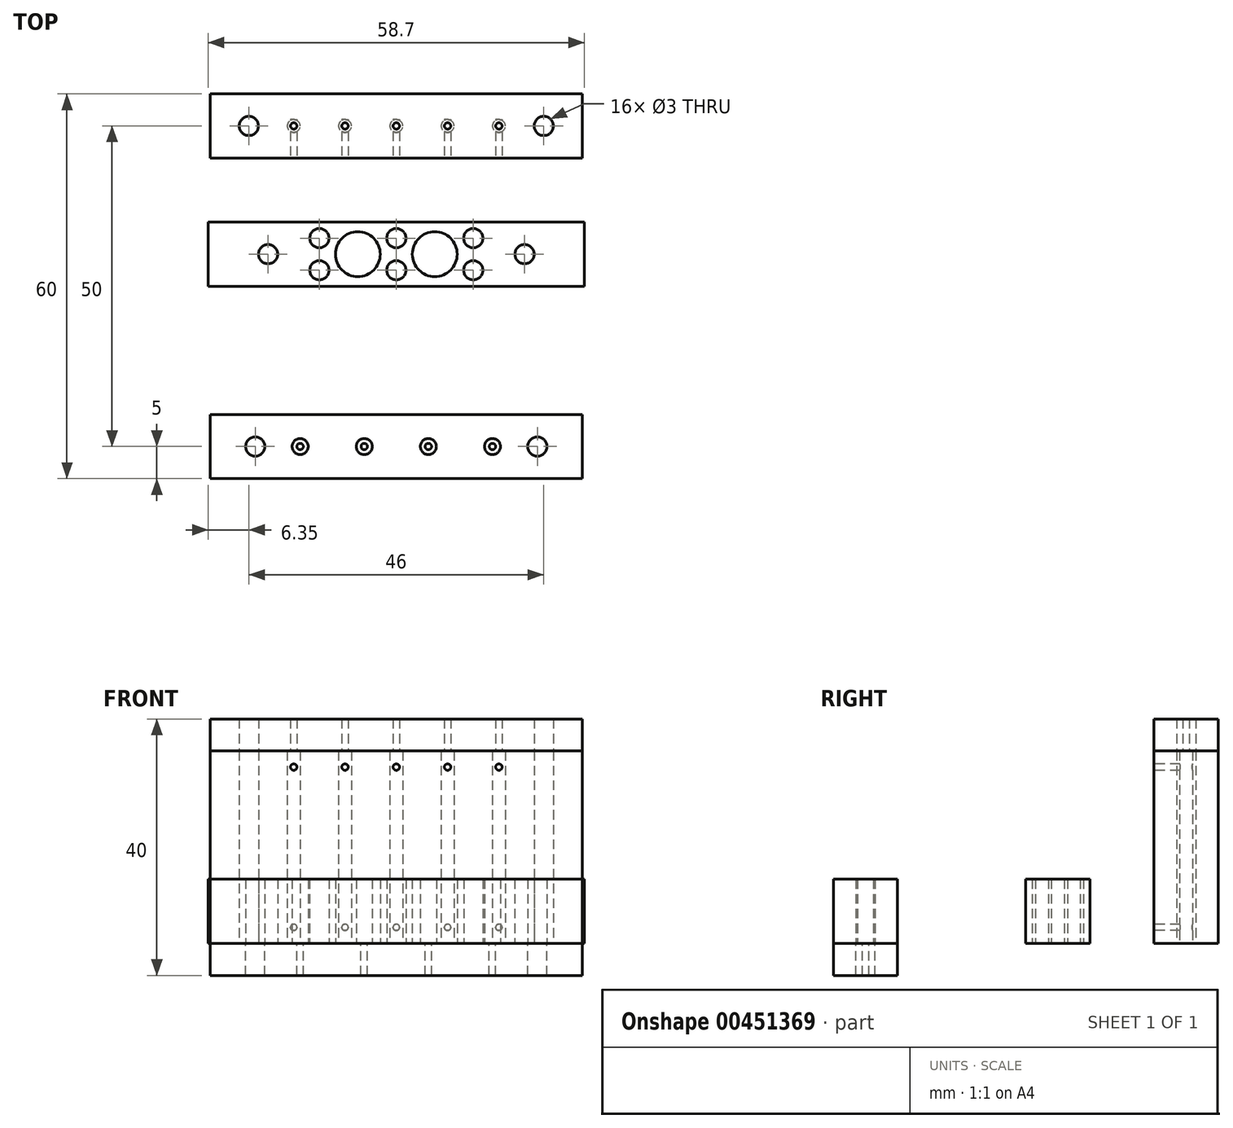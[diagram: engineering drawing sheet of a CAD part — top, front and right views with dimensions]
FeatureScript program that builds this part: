
annotation { "Feature Type Name" : "Feature", "Feature Type Description" : "" }
export const myFeature = defineFeature(function(context is Context, id is Id, definition is map)
    precondition{}
    {
        {
            var Q0;
            Q0=qCreatedBy(makeId("Top.planeOp"),FACE);
            var sketch = newSketch(context, id + "F0", { "sketchPlane" : qUnion([Q0])});
            skLineSegment(sketch, "E0.bottom", {"start": v(29.35, 5) * mm, "end": v(-29.35, 5) * mm});
            skLineSegment(sketch, "E0.top", {"start": v(29.35, -5) * mm, "end": v(-29.35, -5) * mm});
            skLineSegment(sketch, "E0.left", {"start": v(29.35, 5) * mm, "end": v(29.35, -5) * mm});
            skLineSegment(sketch, "E0.right", {"start": v(-29.35, 5) * mm, "end": v(-29.35, -5) * mm});
            skPoint(sketch, "E0.middle", {"position": v(0, 0) * mm});
            skCircle(sketch, "E1", {"center": v(-6, 0) * mm, "radius": 3.5 * mm});
            skPoint(sketch, "E1.centerSnap0", {"position": v(-29.35, 0) * mm});
            skCircle(sketch, "E2.MirrorC", {"center": v(6, 0) * mm, "radius": 3.5 * mm});
            skCircle(sketch, "E3", {"center": v(-12, 2.5) * mm, "radius": 1.5 * mm});
            skCircle(sketch, "E4.0.1.0", {"center": v(-12, -2.5) * mm, "radius": 1.5 * mm});
            skCircle(sketch, "E4.1.0.0", {"center": v(0, 2.5) * mm, "radius": 1.5 * mm});
            skCircle(sketch, "E4.1.1.0", {"center": v(0, -2.5) * mm, "radius": 1.5 * mm});
            skCircle(sketch, "E4.2.0.0", {"center": v(12, 2.5) * mm, "radius": 1.5 * mm});
            skCircle(sketch, "E4.2.1.0", {"center": v(12, -2.5) * mm, "radius": 1.5 * mm});
            skLineSegment(sketch, "E4.direction1", {"start": v(-12, 2.5) * mm, "end": v(0, 2.5) * mm, "construction": true});
            skLineSegment(sketch, "E4.direction2", {"start": v(-12, 2.5) * mm, "end": v(-12, -2.5) * mm, "construction": true});
            skCircle(sketch, "E5", {"center": v(-20, 0) * mm, "radius": 1.5 * mm});
            skCircle(sketch, "E6.MirrorC", {"center": v(20, 0) * mm, "radius": 1.5 * mm});
            skSolve(sketch);
        }
        {
            var Q0;
            Q0=makeQuery(id+"F0.imprint","IMPRINT",FACE,{"disambiguationData":[TD([[makeQuery(id+"F0.imprint","IMPRINT",EDGE,{"derivedFrom":sQuery(id+"F0.wireOp",EDGE,"E0.bottom")}),1.0]])]});
            extrude(context, id + "F1", {"entities" : qUnion([Q0]), "depth" : 10 * mm});
        }
        {
            var Q0;
            Q0=qCreatedBy(makeId("Top.planeOp"),FACE);
            var sketch = newSketch(context, id + "F2", { "sketchPlane" : qUnion([Q0])});
            skLineSegment(sketch, "E7.bottom", {"start": v(29, -25) * mm, "end": v(-29, -25) * mm});
            skLineSegment(sketch, "E7.top", {"start": v(29, -35) * mm, "end": v(-29, -35) * mm});
            skLineSegment(sketch, "E7.left", {"start": v(29, -25) * mm, "end": v(29, -35) * mm});
            skLineSegment(sketch, "E7.right", {"start": v(-29, -25) * mm, "end": v(-29, -35) * mm});
            skPoint(sketch, "E7.middle", {"position": v(0, -30) * mm});
            skLineSegment(sketch, "E8", {"start": v(29, -30) * mm, "end": v(-29, -30) * mm, "construction": true});
            skCircle(sketch, "E9", {"center": v(-15, -30) * mm, "radius": 1.25 * mm});
            skCircle(sketch, "E10", {"center": v(-22, -30) * mm, "radius": 1.5 * mm});
            skCircle(sketch, "E11.1.0.0", {"center": v(-5, -30) * mm, "radius": 1.25 * mm});
            skCircle(sketch, "E11.2.0.0", {"center": v(5, -30) * mm, "radius": 1.25 * mm});
            skCircle(sketch, "E11.3.0.0", {"center": v(15, -30) * mm, "radius": 1.25 * mm});
            skLineSegment(sketch, "E11.direction1", {"start": v(-15, -30) * mm, "end": v(-5, -30) * mm, "construction": true});
            skCircle(sketch, "E12.MirrorC", {"center": v(22, -30) * mm, "radius": 1.5 * mm});
            skSolve(sketch);
        }
        {
            var Q0;
            Q0=makeQuery(id+"F2.imprint","IMPRINT",FACE,{"disambiguationData":[TD([[makeQuery(id+"F2.imprint","IMPRINT",EDGE,{"derivedFrom":sQuery(id+"F2.wireOp",EDGE,"E7.bottom")}),1.0]])]});
            extrude(context, id + "F3", {"entities" : qUnion([Q0]), "depth" : 10 * mm});
        }
        {
            var Q0;
            Q0=makeQuery(id+"F3.opExtrude","CAP_FACE",FACE,{"disambiguationData":[OSD([sQuery(id+"F2.wireOp",EDGE,"E7.bottom"),sQuery(id+"F2.wireOp",EDGE,"E7.top"),sQuery(id+"F2.wireOp",EDGE,"E7.left"),sQuery(id+"F2.wireOp",EDGE,"E7.right"),sQuery(id+"F2.wireOp",EDGE,"E9"),sQuery(id+"F2.wireOp",EDGE,"E10"),sQuery(id+"F2.wireOp",EDGE,"E11.1.0.0"),sQuery(id+"F2.wireOp",EDGE,"E11.2.0.0"),sQuery(id+"F2.wireOp",EDGE,"E11.3.0.0"),sQuery(id+"F2.wireOp",EDGE,"E12.MirrorC")])],"isStart":true});
            var sketch = newSketch(context, id + "F4", { "sketchPlane" : qUnion([Q0])});
            skLineSegment(sketch, "E13.0.0", {"start": v(29, 35) * mm, "end": v(-29, 35) * mm});
            skLineSegment(sketch, "E13.0.1", {"start": v(-29, 35) * mm, "end": v(-29, 25) * mm});
            skLineSegment(sketch, "E13.0.2", {"start": v(-29, 25) * mm, "end": v(29, 25) * mm});
            skLineSegment(sketch, "E13.0.3", {"start": v(29, 25) * mm, "end": v(29, 35) * mm});
            skCircle(sketch, "E14", {"center": v(-22, 30) * mm, "radius": 1.5 * mm});
            skCircle(sketch, "E15", {"center": v(-15, 30) * mm, "radius": 0.5 * mm});
            skCircle(sketch, "E16", {"center": v(-5, 30) * mm, "radius": 0.5 * mm});
            skCircle(sketch, "E17", {"center": v(5, 30) * mm, "radius": 0.5 * mm});
            skCircle(sketch, "E18", {"center": v(15, 30) * mm, "radius": 0.5 * mm});
            skCircle(sketch, "E19", {"center": v(22, 30) * mm, "radius": 1.5 * mm});
            skSolve(sketch);
        }
        {
            var Q0;
            Q0=makeQuery(id+"F4.imprint","IMPRINT",FACE,{"disambiguationData":[TD([[makeQuery(id+"F4.imprint","IMPRINT",EDGE,{"derivedFrom":sQuery(id+"F4.wireOp",EDGE,"E13.0.0")}),1.0]])]});
            var Q1;
            Q1=makeQuery(id+"F4.imprint","IMPRINT",FACE,{"disambiguationData":[TD([[makeQuery(id+"F4.imprint","IMPRINT",EDGE,{"derivedFrom":sQuery(id+"F4.wireOp",EDGE,"E15")}),-1.0]])]});
            var Q2;
            Q2=makeQuery(id+"F4.imprint","IMPRINT",FACE,{"disambiguationData":[TD([[makeQuery(id+"F4.imprint","IMPRINT",EDGE,{"derivedFrom":sQuery(id+"F4.wireOp",EDGE,"E16")}),-1.0]])]});
            var Q3;
            Q3=makeQuery(id+"F4.imprint","IMPRINT",FACE,{"disambiguationData":[TD([[makeQuery(id+"F4.imprint","IMPRINT",EDGE,{"derivedFrom":sQuery(id+"F4.wireOp",EDGE,"E17")}),-1.0]])]});
            var Q4;
            Q4=makeQuery(id+"F4.imprint","IMPRINT",FACE,{"disambiguationData":[TD([[makeQuery(id+"F4.imprint","IMPRINT",EDGE,{"derivedFrom":sQuery(id+"F4.wireOp",EDGE,"E18")}),-1.0]])]});
            extrude(context, id + "F5", {"entities" : qUnion([Q0, Q1, Q2, Q3, Q4]), "depth" : 5 * mm});
        }
        {
            var Q0;
            Q0=qCreatedBy(makeId("Top.planeOp"),FACE);
            var sketch = newSketch(context, id + "F6", { "sketchPlane" : qUnion([Q0])});
            skLineSegment(sketch, "E20.bottom", {"start": v(29, 25) * mm, "end": v(-29, 25) * mm});
            skLineSegment(sketch, "E20.top", {"start": v(29, 15) * mm, "end": v(-29, 15) * mm});
            skLineSegment(sketch, "E20.left", {"start": v(29, 25) * mm, "end": v(29, 15) * mm});
            skLineSegment(sketch, "E20.right", {"start": v(-29, 25) * mm, "end": v(-29, 15) * mm});
            skPoint(sketch, "E20.middle", {"position": v(0, 20) * mm});
            skLineSegment(sketch, "E21", {"start": v(-29, 20) * mm, "end": v(29, 20) * mm, "construction": true});
            skCircle(sketch, "E22", {"center": v(0, 20) * mm, "radius": 1 * mm});
            skCircle(sketch, "E23.1.0.0", {"center": v(8, 20) * mm, "radius": 1 * mm});
            skCircle(sketch, "E23.2.0.0", {"center": v(16, 20) * mm, "radius": 1 * mm});
            skLineSegment(sketch, "E23.direction1", {"start": v(0, 20) * mm, "end": v(8, 20) * mm, "construction": true});
            skCircle(sketch, "E24", {"center": v(23, 20) * mm, "radius": 1.5 * mm});
            skCircle(sketch, "E25.MirrorC", {"center": v(-8, 20) * mm, "radius": 1 * mm});
            skCircle(sketch, "E26.MirrorC", {"center": v(-16, 20) * mm, "radius": 1 * mm});
            skCircle(sketch, "E27.MirrorC", {"center": v(-23, 20) * mm, "radius": 1.5 * mm});
            skSolve(sketch);
        }
        {
            var Q0;
            Q0=makeQuery(id+"F6.imprint","IMPRINT",FACE,{"disambiguationData":[TD([[makeQuery(id+"F6.imprint","IMPRINT",EDGE,{"derivedFrom":sQuery(id+"F6.wireOp",EDGE,"E20.bottom")}),1.0]])]});
            extrude(context, id + "F7", {"entities" : qUnion([Q0]), "depth" : 30 * mm});
        }
        {
            var Q0;
            Q0=makeQuery(id+"F7.opExtrude","CAP_FACE",FACE,{"disambiguationData":[OSD([sQuery(id+"F6.wireOp",EDGE,"E20.bottom"),sQuery(id+"F6.wireOp",EDGE,"E20.top"),sQuery(id+"F6.wireOp",EDGE,"E20.left"),sQuery(id+"F6.wireOp",EDGE,"E20.right"),sQuery(id+"F6.wireOp",EDGE,"E22"),sQuery(id+"F6.wireOp",EDGE,"E23.1.0.0"),sQuery(id+"F6.wireOp",EDGE,"E23.2.0.0"),sQuery(id+"F6.wireOp",EDGE,"E24"),sQuery(id+"F6.wireOp",EDGE,"E25.MirrorC"),sQuery(id+"F6.wireOp",EDGE,"E26.MirrorC"),sQuery(id+"F6.wireOp",EDGE,"E27.MirrorC")])],"isStart":false});
            var sketch = newSketch(context, id + "F8", { "sketchPlane" : qUnion([Q0])});
            skLineSegment(sketch, "E28.0.0", {"start": v(-29, 15) * mm, "end": v(29, 15) * mm});
            skLineSegment(sketch, "E28.0.1", {"start": v(29, 15) * mm, "end": v(29, 25) * mm});
            skLineSegment(sketch, "E28.0.2", {"start": v(29, 25) * mm, "end": v(-29, 25) * mm});
            skLineSegment(sketch, "E28.0.3", {"start": v(-29, 25) * mm, "end": v(-29, 15) * mm});
            skCircle(sketch, "E29", {"center": v(0, 20) * mm, "radius": 0.5 * mm});
            skCircle(sketch, "E30", {"center": v(8, 20) * mm, "radius": 0.5 * mm});
            skCircle(sketch, "E31", {"center": v(16, 20) * mm, "radius": 0.5 * mm});
            skCircle(sketch, "E32", {"center": v(-8, 20) * mm, "radius": 0.5 * mm});
            skCircle(sketch, "E33", {"center": v(-16, 20) * mm, "radius": 0.5 * mm});
            skCircle(sketch, "E34", {"center": v(-23, 20) * mm, "radius": 1.5 * mm});
            skCircle(sketch, "E35", {"center": v(23, 20) * mm, "radius": 1.5 * mm});
            skSolve(sketch);
        }
        {
            var Q0;
            Q0=makeQuery(id+"F8.imprint","IMPRINT",FACE,{"disambiguationData":[TD([[makeQuery(id+"F8.imprint","IMPRINT",EDGE,{"derivedFrom":sQuery(id+"F8.wireOp",EDGE,"E28.0.0")}),-1.0]])]});
            var Q1;
            Q1=makeQuery(id+"F8.imprint","IMPRINT",FACE,{"disambiguationData":[TD([[makeQuery(id+"F8.imprint","IMPRINT",EDGE,{"derivedFrom":sQuery(id+"F8.wireOp",EDGE,"E33")}),-1.0]])]});
            var Q2;
            Q2=makeQuery(id+"F8.imprint","IMPRINT",FACE,{"disambiguationData":[TD([[makeQuery(id+"F8.imprint","IMPRINT",EDGE,{"derivedFrom":sQuery(id+"F8.wireOp",EDGE,"E32")}),-1.0]])]});
            var Q3;
            Q3=makeQuery(id+"F8.imprint","IMPRINT",FACE,{"disambiguationData":[TD([[makeQuery(id+"F8.imprint","IMPRINT",EDGE,{"derivedFrom":sQuery(id+"F8.wireOp",EDGE,"E29")}),-1.0]])]});
            var Q4;
            Q4=makeQuery(id+"F8.imprint","IMPRINT",FACE,{"disambiguationData":[TD([[makeQuery(id+"F8.imprint","IMPRINT",EDGE,{"derivedFrom":sQuery(id+"F8.wireOp",EDGE,"E30")}),-1.0]])]});
            var Q5;
            Q5=makeQuery(id+"F8.imprint","IMPRINT",FACE,{"disambiguationData":[TD([[makeQuery(id+"F8.imprint","IMPRINT",EDGE,{"derivedFrom":sQuery(id+"F8.wireOp",EDGE,"E31")}),-1.0]])]});
            extrude(context, id + "F9", {"entities" : qUnion([Q0, Q1, Q2, Q3, Q4, Q5]), "depth" : 5 * mm});
        }
        {
            var Q0;
            Q0=makeQuery(id+"F7.opExtrude","SWEPT_FACE",FACE,{"disambiguationData":[OSD([sQuery(id+"F6.wireOp",EDGE,"E20.top")])]});
            var sketch = newSketch(context, id + "F10", { "sketchPlane" : qUnion([Q0])});
            skCircle(sketch, "E36", {"center": v(0, 2.5) * mm, "radius": 0.5 * mm});
            skCircle(sketch, "E37.0.1.0", {"center": v(0, 27.5) * mm, "radius": 0.5 * mm});
            skCircle(sketch, "E37.1.0.0", {"center": v(8, 2.5) * mm, "radius": 0.5 * mm});
            skCircle(sketch, "E37.1.1.0", {"center": v(8, 27.5) * mm, "radius": 0.5 * mm});
            skCircle(sketch, "E37.2.0.0", {"center": v(16, 2.5) * mm, "radius": 0.5 * mm});
            skCircle(sketch, "E37.2.1.0", {"center": v(16, 27.5) * mm, "radius": 0.5 * mm});
            skLineSegment(sketch, "E37.direction1", {"start": v(0, 2.5) * mm, "end": v(8, 2.5) * mm, "construction": true});
            skLineSegment(sketch, "E37.direction2", {"start": v(0, 2.5) * mm, "end": v(0, 27.5) * mm, "construction": true});
            skCircle(sketch, "E38.MirrorC", {"center": v(-8, 2.5) * mm, "radius": 0.5 * mm});
            skCircle(sketch, "E39.MirrorC", {"center": v(-16, 27.5) * mm, "radius": 0.5 * mm});
            skCircle(sketch, "E40.MirrorC", {"center": v(-16, 2.5) * mm, "radius": 0.5 * mm});
            skCircle(sketch, "E41.MirrorC", {"center": v(-8, 27.5) * mm, "radius": 0.5 * mm});
            skSolve(sketch);
        }
        {
            var Q0;
            Q0 = qSketchRegion(id + "F10", true);
            extrude(context, id + "F11", {"entities" : qUnion([Q0]), "operationType" : NewBodyOperationType.REMOVE, "oppositeDirection" : true, "depth" : 6 * mm});
        }
    });
